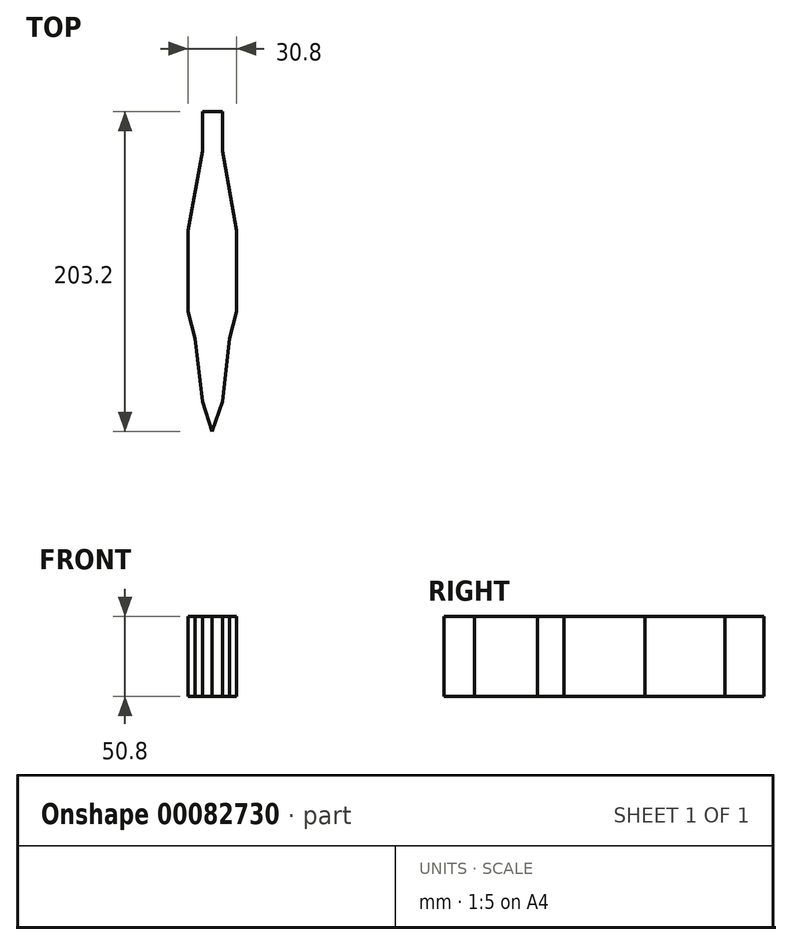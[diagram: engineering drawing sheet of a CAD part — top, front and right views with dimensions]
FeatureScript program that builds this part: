
annotation { "Feature Type Name" : "Feature", "Feature Type Description" : "" }
export const myFeature = defineFeature(function(context is Context, id is Id, definition is map)
    precondition{}
    {
        {
            var Q0;
            Q0=qCreatedBy(makeId("Top.planeOp"),FACE);
            var sketch = newSketch(context, id + "F0", { "sketchPlane" : qUnion([Q0])});
            skLineSegment(sketch, "E0.bottom", {"start": v(63.5, 101.6) * mm, "end": v(-63.5, 101.6) * mm});
            skLineSegment(sketch, "E0.top", {"start": v(63.5, -101.6) * mm, "end": v(-63.5, -101.6) * mm});
            skLineSegment(sketch, "E0.left", {"start": v(63.5, 101.6) * mm, "end": v(63.5, -101.6) * mm});
            skLineSegment(sketch, "E0.right", {"start": v(-63.5, 101.6) * mm, "end": v(-63.5, -101.6) * mm});
            skPoint(sketch, "E0.middle", {"position": v(0, 0) * mm});
            skSolve(sketch);
        }
        {
            var Q0;
            Q0 = qSketchRegion(id + "F0", true);
            extrude(context, id + "F1", {"entities" : qUnion([Q0]), "depth" : 101.6 * mm});
        }
        {
            var Q0;
            Q0=makeQuery(id+"F1.opExtrude","CAP_FACE",FACE,{"disambiguationData":[OSD([sQuery(id+"F0.wireOp",EDGE,"E0.bottom"),sQuery(id+"F0.wireOp",EDGE,"E0.top"),sQuery(id+"F0.wireOp",EDGE,"E0.left"),sQuery(id+"F0.wireOp",EDGE,"E0.right")])],"isStart":false});
            var sketch = newSketch(context, id + "F2", { "sketchPlane" : qUnion([Q0])});
            skLineSegment(sketch, "E1.bottom", {"start": v(6.35, 25.4) * mm, "end": v(-6.35, 25.4) * mm});
            skLineSegment(sketch, "E1.top", {"start": v(6.35, -25.4) * mm, "end": v(-6.35, -25.4) * mm});
            skLineSegment(sketch, "E1.left", {"start": v(6.35, 25.4) * mm, "end": v(6.35, -25.4) * mm});
            skLineSegment(sketch, "E1.right", {"start": v(-6.35, 25.4) * mm, "end": v(-6.35, -25.4) * mm});
            skPoint(sketch, "E1.middle", {"position": v(0, 0) * mm});
            skLineSegment(sketch, "E2", {"start": v(-6.35, -25.4) * mm, "end": v(-6.35, -59.46) * mm});
            skLineSegment(sketch, "E3", {"start": v(-6.35, -59.46) * mm, "end": v(-15.4, -25.4) * mm});
            skLineSegment(sketch, "E4", {"start": v(-15.4, -25.4) * mm, "end": v(-15.4, 25.88) * mm});
            skLineSegment(sketch, "E5", {"start": v(-15.4, 25.88) * mm, "end": v(-6.35, 76.63) * mm});
            skLineSegment(sketch, "E6", {"start": v(-6.35, 76.63) * mm, "end": v(-6.35, 101.6) * mm});
            skPoint(sketch, "E7.endSnap0", {"position": v(0, 101.6) * mm});
            skLineSegment(sketch, "E8", {"start": v(0, 101.6) * mm, "end": v(0, -101.6) * mm, "construction": true});
            skLineSegment(sketch, "E9.MirrorCS", {"start": v(6.35, 76.63) * mm, "end": v(6.35, 101.6) * mm});
            skLineSegment(sketch, "E10.MirrorCS", {"start": v(15.4, 25.88) * mm, "end": v(6.35, 76.63) * mm});
            skLineSegment(sketch, "E11.MirrorCS", {"start": v(15.4, -25.4) * mm, "end": v(15.4, 25.88) * mm});
            skLineSegment(sketch, "E12.MirrorCS", {"start": v(6.35, -59.46) * mm, "end": v(15.4, -25.4) * mm});
            skLineSegment(sketch, "E13.MirrorCS", {"start": v(6.35, -25.4) * mm, "end": v(6.35, -59.46) * mm});
            skLineSegment(sketch, "E14", {"start": v(10.88, -42.43) * mm, "end": v(6.35, -82.44) * mm});
            skLineSegment(sketch, "E15", {"start": v(6.35, -82.44) * mm, "end": v(0, -101.6) * mm});
            skLineSegment(sketch, "E16.MirrorCS", {"start": v(-10.88, -42.43) * mm, "end": v(-6.35, -82.44) * mm});
            skLineSegment(sketch, "E17.MirrorCS", {"start": v(-6.35, -82.44) * mm, "end": v(0, -101.6) * mm});
            skSolve(sketch);
        }
        {
            var Q0;
            {var subQ2=sQuery(id+"F2.wireOp",EDGE,"E4");Q0=makeQuery(id+"F2.imprint","IMPRINT",FACE,{"disambiguationData":[TD([[makeQuery(id+"F2.imprint","IMPRINT",EDGE,{"derivedFrom":subQ2}),1.0]])]});}
            var Q1;
            {var subQ4=sQuery(id+"F2.wireOp",EDGE,"E9.MirrorCS");Q1=makeQuery(id+"F2.imprint","IMPRINT",FACE,{"disambiguationData":[TD([[makeQuery(id+"F2.imprint","IMPRINT",EDGE,{"derivedFrom":subQ4}),-1.0]])]});}
            extrude(context, id + "F3", {"entities" : qUnion([Q0, Q1]), "operationType" : NewBodyOperationType.REMOVE, "oppositeDirection" : true, "depth" : 50.8 * mm});
        }
        {
            var Q0;
            Q0=makeQuery(id+"F1.opExtrude","SWEPT_FACE",FACE,{"disambiguationData":[OSD([sQuery(id+"F0.wireOp",EDGE,"E0.left")])]});
            extrude(context, id + "F4", {"entities" : qUnion([Q0]), "operationType" : NewBodyOperationType.REMOVE, "endBound" : BoundingType.THROUGH_ALL, "oppositeDirection" : true, "depth" : 25.4 * mm});
        }
    });
